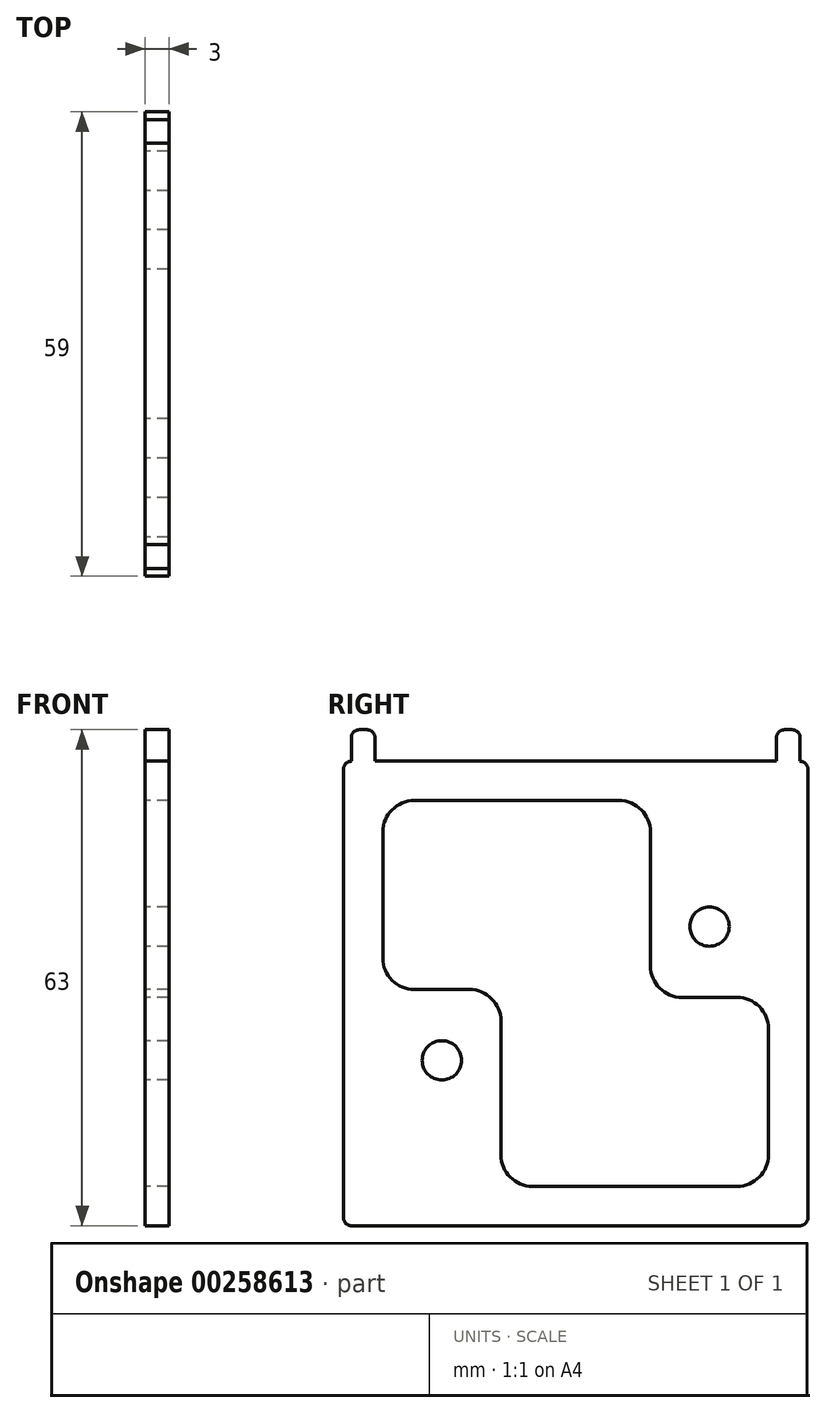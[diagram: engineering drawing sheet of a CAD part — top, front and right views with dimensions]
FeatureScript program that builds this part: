
annotation { "Feature Type Name" : "Feature", "Feature Type Description" : "" }
export const myFeature = defineFeature(function(context is Context, id is Id, definition is map)
    precondition{}
    {
        {
            var Q0;
            Q0=qCreatedBy(makeId("Right.planeOp"),FACE);
            var sketch = newSketch(context, id + "F0", { "sketchPlane" : qUnion([Q0])});
            skLineSegment(sketch, "E0.bottom", {"start": v(-29.5, 29.5) * mm, "end": v(29.5, 29.5) * mm});
            skLineSegment(sketch, "E0.top", {"start": v(-29.5, -29.5) * mm, "end": v(29.5, -29.5) * mm});
            skLineSegment(sketch, "E0.left", {"start": v(-29.5, 29.5) * mm, "end": v(-29.5, -29.5) * mm});
            skLineSegment(sketch, "E0.right", {"start": v(29.5, 29.5) * mm, "end": v(29.5, -29.5) * mm});
            skPoint(sketch, "E0.middle", {"position": v(0, 0) * mm});
            skLineSegment(sketch, "E1", {"start": v(-29.5, -29.5) * mm, "end": v(-28.5, -29.5) * mm, "construction": true});
            skLineSegment(sketch, "E2.bottom", {"start": v(-28.5, -29.5) * mm, "end": v(-25.5, -29.5) * mm});
            skLineSegment(sketch, "E2.top", {"start": v(-28.5, -33.5) * mm, "end": v(-25.5, -33.5) * mm});
            skLineSegment(sketch, "E2.left", {"start": v(-28.5, -29.5) * mm, "end": v(-28.5, -33.5) * mm});
            skLineSegment(sketch, "E2.right", {"start": v(-25.5, -29.5) * mm, "end": v(-25.5, -33.5) * mm});
            skLineSegment(sketch, "E3", {"start": v(29.5, -29.5) * mm, "end": v(28.5, -29.5) * mm, "construction": true});
            skLineSegment(sketch, "E4.bottom", {"start": v(28.5, -29.5) * mm, "end": v(25.5, -29.5) * mm});
            skLineSegment(sketch, "E4.top", {"start": v(28.5, -33.5) * mm, "end": v(25.5, -33.5) * mm});
            skLineSegment(sketch, "E4.left", {"start": v(28.5, -29.5) * mm, "end": v(28.5, -33.5) * mm});
            skLineSegment(sketch, "E4.right", {"start": v(25.5, -29.5) * mm, "end": v(25.5, -33.5) * mm});
            skLineSegment(sketch, "E5.1.0", {"start": v(-28.5, 33.5) * mm, "end": v(-25.5, 33.5) * mm});
            skLineSegment(sketch, "E5.1.1", {"start": v(-29.5, 29.5) * mm, "end": v(-28.5, 29.5) * mm, "construction": true});
            skLineSegment(sketch, "E5.1.2", {"start": v(-28.5, 29.5) * mm, "end": v(-28.5, 33.5) * mm});
            skLineSegment(sketch, "E5.1.3", {"start": v(-28.5, 29.5) * mm, "end": v(-25.5, 29.5) * mm});
            skLineSegment(sketch, "E5.1.4", {"start": v(-25.5, 29.5) * mm, "end": v(-25.5, 33.5) * mm});
            skLineSegment(sketch, "E5.anchor1", {"start": v(0, 0) * mm, "end": v(25.5, -33.5) * mm, "construction": true});
            skLineSegment(sketch, "E5.anchor2", {"start": v(0, 0) * mm, "end": v(-25.5, 33.5) * mm, "construction": true});
            skLineSegment(sketch, "E6.1.0", {"start": v(28.5, 33.5) * mm, "end": v(25.5, 33.5) * mm});
            skLineSegment(sketch, "E6.1.1", {"start": v(28.5, 29.5) * mm, "end": v(25.5, 29.5) * mm});
            skLineSegment(sketch, "E6.1.2", {"start": v(29.5, 29.5) * mm, "end": v(28.5, 29.5) * mm, "construction": true});
            skLineSegment(sketch, "E6.1.3", {"start": v(28.5, 29.5) * mm, "end": v(28.5, 33.5) * mm});
            skLineSegment(sketch, "E6.1.4", {"start": v(25.5, 29.5) * mm, "end": v(25.5, 33.5) * mm});
            skLineSegment(sketch, "E7.bottom", {"start": v(-29.5, -29.5) * mm, "end": v(-24.5, -29.5) * mm, "construction": true});
            skLineSegment(sketch, "E8.bottom", {"start": v(24, 11.5) * mm, "end": v(-24, 11.5) * mm, "construction": true});
            skLineSegment(sketch, "E8.top", {"start": v(24, -11.5) * mm, "end": v(-24, -11.5) * mm, "construction": true});
            skLineSegment(sketch, "E8.left", {"start": v(24, 11.5) * mm, "end": v(24, -11.5) * mm, "construction": true});
            skLineSegment(sketch, "E8.right", {"start": v(-24, 11.5) * mm, "end": v(-24, -11.5) * mm, "construction": true});
            skLineSegment(sketch, "E9.bottom", {"start": v(24, 11.5) * mm, "end": v(17, 11.5) * mm, "construction": true});
            skLineSegment(sketch, "E9.top", {"start": v(24, 8.5) * mm, "end": v(17, 8.5) * mm, "construction": true});
            skLineSegment(sketch, "E9.left", {"start": v(24, 11.5) * mm, "end": v(24, 8.5) * mm, "construction": true});
            skLineSegment(sketch, "E9.right", {"start": v(17, 11.5) * mm, "end": v(17, 8.5) * mm, "construction": true});
            skLineSegment(sketch, "E10.bottom", {"start": v(-24, -11.5) * mm, "end": v(-17, -11.5) * mm, "construction": true});
            skLineSegment(sketch, "E10.top", {"start": v(-24, -8.5) * mm, "end": v(-17, -8.5) * mm, "construction": true});
            skLineSegment(sketch, "E10.left", {"start": v(-24, -11.5) * mm, "end": v(-24, -8.5) * mm, "construction": true});
            skLineSegment(sketch, "E10.right", {"start": v(-17, -11.5) * mm, "end": v(-17, -8.5) * mm, "construction": true});
            skCircle(sketch, "E11", {"center": v(17, 8.5) * mm, "radius": 2.5 * mm});
            skCircle(sketch, "E12", {"center": v(-17, -8.5) * mm, "radius": 2.5 * mm});
            skLineSegment(sketch, "E13.bottom", {"start": v(-24.5, 24.5) * mm, "end": v(24.5, 24.5) * mm});
            skLineSegment(sketch, "E13.top", {"start": v(-24.5, -24.5) * mm, "end": v(24.5, -24.5) * mm});
            skLineSegment(sketch, "E13.left", {"start": v(-24.5, 24.5) * mm, "end": v(-24.5, -24.5) * mm});
            skLineSegment(sketch, "E13.right", {"start": v(24.5, 24.5) * mm, "end": v(24.5, -24.5) * mm});
            skLineSegment(sketch, "E14.bottom", {"start": v(-24.5, -24.5) * mm, "end": v(-9.5, -24.5) * mm});
            skLineSegment(sketch, "E14.top", {"start": v(-24.5, 0.5) * mm, "end": v(-9.5, 0.5) * mm});
            skLineSegment(sketch, "E14.left", {"start": v(-24.5, -24.5) * mm, "end": v(-24.5, 0.5) * mm});
            skLineSegment(sketch, "E14.right", {"start": v(-9.5, -24.5) * mm, "end": v(-9.5, 0.5) * mm});
            skLineSegment(sketch, "E15.bottom", {"start": v(24.5, 24.5) * mm, "end": v(9.5, 24.5) * mm});
            skLineSegment(sketch, "E15.top", {"start": v(24.5, -0.5) * mm, "end": v(9.5, -0.5) * mm});
            skLineSegment(sketch, "E15.left", {"start": v(24.5, 24.5) * mm, "end": v(24.5, -0.5) * mm});
            skLineSegment(sketch, "E15.right", {"start": v(9.5, 24.5) * mm, "end": v(9.5, -0.5) * mm});
            skSolve(sketch);
        }
        {
            var Q0;
            {var subQ1=sQuery(id+"F0.wireOp",EDGE,"E0.left");Q0=makeQuery(id+"F0.imprint","IMPRINT",FACE,{"disambiguationData":[TD([[makeQuery(id+"F0.imprint","IMPRINT",EDGE,{"derivedFrom":subQ1}),1.0]])]});}
            var Q1;
            Q1=makeQuery(id+"F0.imprint","IMPRINT",FACE,{"disambiguationData":[TD([[makeQuery(id+"F0.imprint","IMPRINT",EDGE,{"derivedFrom":sQuery(id+"F0.wireOp",EDGE,"E5.1.0")}),-1.0]])]});
            var Q2;
            Q2=makeQuery(id+"F0.imprint","IMPRINT",FACE,{"disambiguationData":[TD([[makeQuery(id+"F0.imprint","IMPRINT",EDGE,{"derivedFrom":sQuery(id+"F0.wireOp",EDGE,"E6.1.0")}),1.0]])]});
            var Q3;
            Q3=makeQuery(id+"F0.imprint","IMPRINT",FACE,{"disambiguationData":[TD([[makeQuery(id+"F0.imprint","IMPRINT",EDGE,{"derivedFrom":sQuery(id+"F0.wireOp",EDGE,"E2.bottom")}),-1.0]])]});
            var Q4;
            Q4=makeQuery(id+"F0.imprint","IMPRINT",FACE,{"disambiguationData":[TD([[makeQuery(id+"F0.imprint","IMPRINT",EDGE,{"derivedFrom":sQuery(id+"F0.wireOp",EDGE,"E4.bottom")}),1.0]])]});
            var Q5;
            Q5=makeQuery(id+"F0.imprint","IMPRINT",FACE,{"disambiguationData":[TD([[makeQuery(id+"F0.imprint","IMPRINT",EDGE,{"derivedFrom":sQuery(id+"F0.wireOp",EDGE,"E12")}),-1.0]])]});
            var Q6;
            Q6=makeQuery(id+"F0.imprint","IMPRINT",FACE,{"disambiguationData":[TD([[makeQuery(id+"F0.imprint","IMPRINT",EDGE,{"derivedFrom":sQuery(id+"F0.wireOp",EDGE,"E11")}),-1.0]])]});
            extrude(context, id + "F1", {"entities" : qUnion([Q0, Q1, Q2, Q3, Q4, Q5, Q6]), "depth" : 4 * mm});
        }
        {
            var Q0;
            Q0=makeQuery(id+"F1.opExtrude","CAP_FACE",FACE,{"disambiguationData":[OSD([sQuery(id+"F0.wireOp",EDGE,"E0.bottom"),sQuery(id+"F0.wireOp",EDGE,"E0.top"),sQuery(id+"F0.wireOp",EDGE,"E0.left"),sQuery(id+"F0.wireOp",EDGE,"E0.right"),sQuery(id+"F0.wireOp",EDGE,"E2.top"),sQuery(id+"F0.wireOp",EDGE,"E2.left"),sQuery(id+"F0.wireOp",EDGE,"E2.right"),sQuery(id+"F0.wireOp",EDGE,"E4.top"),sQuery(id+"F0.wireOp",EDGE,"E4.left"),sQuery(id+"F0.wireOp",EDGE,"E4.right"),sQuery(id+"F0.wireOp",EDGE,"E5.1.0"),sQuery(id+"F0.wireOp",EDGE,"E5.1.2"),sQuery(id+"F0.wireOp",EDGE,"E5.1.4"),sQuery(id+"F0.wireOp",EDGE,"E6.1.0"),sQuery(id+"F0.wireOp",EDGE,"E6.1.3"),sQuery(id+"F0.wireOp",EDGE,"E6.1.4"),sQuery(id+"F0.wireOp",EDGE,"E11"),sQuery(id+"F0.wireOp",EDGE,"E12"),sQuery(id+"F0.wireOp",EDGE,"E13.bottom"),sQuery(id+"F0.wireOp",EDGE,"E13.top"),sQuery(id+"F0.wireOp",EDGE,"E13.left"),sQuery(id+"F0.wireOp",EDGE,"E13.right"),sQuery(id+"F0.wireOp",EDGE,"E14.top"),sQuery(id+"F0.wireOp",EDGE,"E14.right"),sQuery(id+"F0.wireOp",EDGE,"E15.top"),sQuery(id+"F0.wireOp",EDGE,"E15.right")])],"isStart":true});
            var sketch = newSketch(context, id + "F2", { "sketchPlane" : qUnion([Q0])});
            skLineSegment(sketch, "E16.bottom", {"start": v(-28.5, 33.5) * mm, "end": v(-25.5, 33.5) * mm});
            skLineSegment(sketch, "E16.top", {"start": v(-28.5, 29.5) * mm, "end": v(-25.5, 29.5) * mm});
            skLineSegment(sketch, "E16.left", {"start": v(-28.5, 33.5) * mm, "end": v(-28.5, 29.5) * mm});
            skLineSegment(sketch, "E16.right", {"start": v(-25.5, 33.5) * mm, "end": v(-25.5, 29.5) * mm});
            skLineSegment(sketch, "E17.bottom", {"start": v(25.5, 33.5) * mm, "end": v(28.5, 33.5) * mm});
            skLineSegment(sketch, "E17.top", {"start": v(25.5, 29.5) * mm, "end": v(28.5, 29.5) * mm});
            skLineSegment(sketch, "E17.left", {"start": v(25.5, 33.5) * mm, "end": v(25.5, 29.5) * mm});
            skLineSegment(sketch, "E17.right", {"start": v(28.5, 33.5) * mm, "end": v(28.5, 29.5) * mm});
            skLineSegment(sketch, "E18.bottom", {"start": v(-28.5, -33.5) * mm, "end": v(-25.5, -33.5) * mm});
            skLineSegment(sketch, "E18.top", {"start": v(-28.5, -29.5) * mm, "end": v(-25.5, -29.5) * mm});
            skLineSegment(sketch, "E18.left", {"start": v(-28.5, -33.5) * mm, "end": v(-28.5, -29.5) * mm});
            skLineSegment(sketch, "E18.right", {"start": v(-25.5, -33.5) * mm, "end": v(-25.5, -29.5) * mm});
            skLineSegment(sketch, "E19.bottom", {"start": v(25.5, -29.5) * mm, "end": v(28.5, -29.5) * mm});
            skLineSegment(sketch, "E19.top", {"start": v(25.5, -33.5) * mm, "end": v(28.5, -33.5) * mm});
            skLineSegment(sketch, "E19.left", {"start": v(25.5, -29.5) * mm, "end": v(25.5, -33.5) * mm});
            skLineSegment(sketch, "E19.right", {"start": v(28.5, -29.5) * mm, "end": v(28.5, -33.5) * mm});
            skSolve(sketch);
        }
        {
            var Q0;
            Q0=makeQuery(id+"F2.imprint","IMPRINT",FACE,{"disambiguationData":[TD([[makeQuery(id+"F2.imprint","IMPRINT",EDGE,{"derivedFrom":sQuery(id+"F2.wireOp",EDGE,"E16.bottom")}),-1.0]])]});
            var Q1;
            Q1=makeQuery(id+"F2.imprint","IMPRINT",FACE,{"disambiguationData":[TD([[makeQuery(id+"F2.imprint","IMPRINT",EDGE,{"derivedFrom":sQuery(id+"F2.wireOp",EDGE,"E17.bottom")}),1.0]])]});
            var Q2;
            Q2=makeQuery(id+"F2.imprint","IMPRINT",FACE,{"disambiguationData":[TD([[makeQuery(id+"F2.imprint","IMPRINT",EDGE,{"derivedFrom":sQuery(id+"F2.wireOp",EDGE,"E18.bottom")}),1.0]])]});
            var Q3;
            Q3=makeQuery(id+"F2.imprint","IMPRINT",FACE,{"disambiguationData":[TD([[makeQuery(id+"F2.imprint","IMPRINT",EDGE,{"derivedFrom":sQuery(id+"F2.wireOp",EDGE,"E19.bottom")}),-1.0]])]});
            extrude(context, id + "F3", {"entities" : qUnion([Q0, Q1, Q2, Q3]), "operationType" : NewBodyOperationType.REMOVE, "oppositeDirection" : true, "depth" : 1 * mm});
        }
        {
            var Q0;
            Q0=makeQuery(id+"F1.opExtrude","SWEPT_EDGE",EDGE,{"disambiguationData":[OSD([sQuery(id+"F0.wireOp",EDGE,"E15.top"),sQuery(id+"F0.wireOp",EDGE,"E15.right")])]});
            var Q1;
            Q1=makeQuery(id+"F1.opExtrude","SWEPT_EDGE",EDGE,{"disambiguationData":[OSD([sQuery(id+"F0.wireOp",EDGE,"E13.bottom"),sQuery(id+"F0.wireOp",EDGE,"E15.bottom"),sQuery(id+"F0.wireOp",EDGE,"E15.right")])]});
            var Q2;
            Q2=makeQuery(id+"F1.opExtrude","SWEPT_EDGE",EDGE,{"disambiguationData":[OSD([sQuery(id+"F0.wireOp",EDGE,"E13.right"),sQuery(id+"F0.wireOp",EDGE,"E15.top"),sQuery(id+"F0.wireOp",EDGE,"E15.left")])]});
            var Q3;
            Q3=makeQuery(id+"F1.opExtrude","SWEPT_EDGE",EDGE,{"disambiguationData":[OSD([sQuery(id+"F0.wireOp",EDGE,"E14.top"),sQuery(id+"F0.wireOp",EDGE,"E14.right")])]});
            var Q4;
            Q4=makeQuery(id+"F1.opExtrude","SWEPT_EDGE",EDGE,{"disambiguationData":[OSD([sQuery(id+"F0.wireOp",EDGE,"E13.left"),sQuery(id+"F0.wireOp",EDGE,"E14.top"),sQuery(id+"F0.wireOp",EDGE,"E14.left")])]});
            var Q5;
            Q5=makeQuery(id+"F1.opExtrude","SWEPT_EDGE",EDGE,{"disambiguationData":[OSD([sQuery(id+"F0.wireOp",EDGE,"E13.top"),sQuery(id+"F0.wireOp",EDGE,"E14.bottom"),sQuery(id+"F0.wireOp",EDGE,"E14.right")])]});
            var Q6;
            Q6=makeQuery(id+"F1.opExtrude","SWEPT_EDGE",EDGE,{"disambiguationData":[OSD([sQuery(id+"F0.wireOp",EDGE,"E13.bottom"),sQuery(id+"F0.wireOp",EDGE,"E13.left")])]});
            var Q7;
            Q7=makeQuery(id+"F1.opExtrude","SWEPT_EDGE",EDGE,{"disambiguationData":[OSD([sQuery(id+"F0.wireOp",EDGE,"E13.top"),sQuery(id+"F0.wireOp",EDGE,"E13.right")])]});
            fillet(context, id + "F4", {"entities" : qUnion([Q0, Q1, Q2, Q3, Q4, Q5, Q6, Q7]), "radius" : 4 * mm, "tangentPropagation" : true, "allowEdgeOverflow" : false});
        }
        {
            var Q0;
            Q0=makeQuery(id+"F1.opExtrude","SWEPT_EDGE",EDGE,{"disambiguationData":[OSD([sQuery(id+"F0.wireOp",EDGE,"E6.1.0"),sQuery(id+"F0.wireOp",EDGE,"E6.1.3")])]});
            var Q1;
            Q1=makeQuery(id+"F1.opExtrude","SWEPT_EDGE",EDGE,{"disambiguationData":[OSD([sQuery(id+"F0.wireOp",EDGE,"E6.1.0"),sQuery(id+"F0.wireOp",EDGE,"E6.1.4")])]});
            var Q2;
            Q2=makeQuery(id+"F1.opExtrude","SWEPT_EDGE",EDGE,{"disambiguationData":[OSD([sQuery(id+"F0.wireOp",EDGE,"E5.1.0"),sQuery(id+"F0.wireOp",EDGE,"E5.1.4")])]});
            var Q3;
            Q3=makeQuery(id+"F1.opExtrude","SWEPT_EDGE",EDGE,{"disambiguationData":[OSD([sQuery(id+"F0.wireOp",EDGE,"E5.1.0"),sQuery(id+"F0.wireOp",EDGE,"E5.1.2")])]});
            var Q4;
            Q4=makeQuery(id+"F1.opExtrude","SWEPT_EDGE",EDGE,{"disambiguationData":[OSD([sQuery(id+"F0.wireOp",EDGE,"E0.bottom"),sQuery(id+"F0.wireOp",EDGE,"E0.right")])]});
            var Q5;
            Q5=makeQuery(id+"F1.opExtrude","SWEPT_EDGE",EDGE,{"disambiguationData":[OSD([sQuery(id+"F0.wireOp",EDGE,"E0.bottom"),sQuery(id+"F0.wireOp",EDGE,"E0.left")])]});
            var Q6;
            Q6=makeQuery(id+"F1.opExtrude","SWEPT_EDGE",EDGE,{"disambiguationData":[OSD([sQuery(id+"F0.wireOp",EDGE,"E0.top"),sQuery(id+"F0.wireOp",EDGE,"E0.left")])]});
            var Q7;
            Q7=makeQuery(id+"F1.opExtrude","SWEPT_EDGE",EDGE,{"disambiguationData":[OSD([sQuery(id+"F0.wireOp",EDGE,"E2.top"),sQuery(id+"F0.wireOp",EDGE,"E2.left")])]});
            var Q8;
            Q8=makeQuery(id+"F1.opExtrude","SWEPT_EDGE",EDGE,{"disambiguationData":[OSD([sQuery(id+"F0.wireOp",EDGE,"E2.top"),sQuery(id+"F0.wireOp",EDGE,"E2.right")])]});
            var Q9;
            Q9=makeQuery(id+"F1.opExtrude","SWEPT_EDGE",EDGE,{"disambiguationData":[OSD([sQuery(id+"F0.wireOp",EDGE,"E0.top"),sQuery(id+"F0.wireOp",EDGE,"E0.right")])]});
            var Q10;
            Q10=makeQuery(id+"F1.opExtrude","SWEPT_EDGE",EDGE,{"disambiguationData":[OSD([sQuery(id+"F0.wireOp",EDGE,"E4.top"),sQuery(id+"F0.wireOp",EDGE,"E4.left")])]});
            var Q11;
            Q11=makeQuery(id+"F1.opExtrude","SWEPT_EDGE",EDGE,{"disambiguationData":[OSD([sQuery(id+"F0.wireOp",EDGE,"E4.top"),sQuery(id+"F0.wireOp",EDGE,"E4.right")])]});
            fillet(context, id + "F5", {"entities" : qUnion([Q0, Q1, Q2, Q3, Q4, Q5, Q6, Q7, Q8, Q9, Q10, Q11]), "radius" : 1 * mm, "tangentPropagation" : true, "allowEdgeOverflow" : false});
        }
    });
